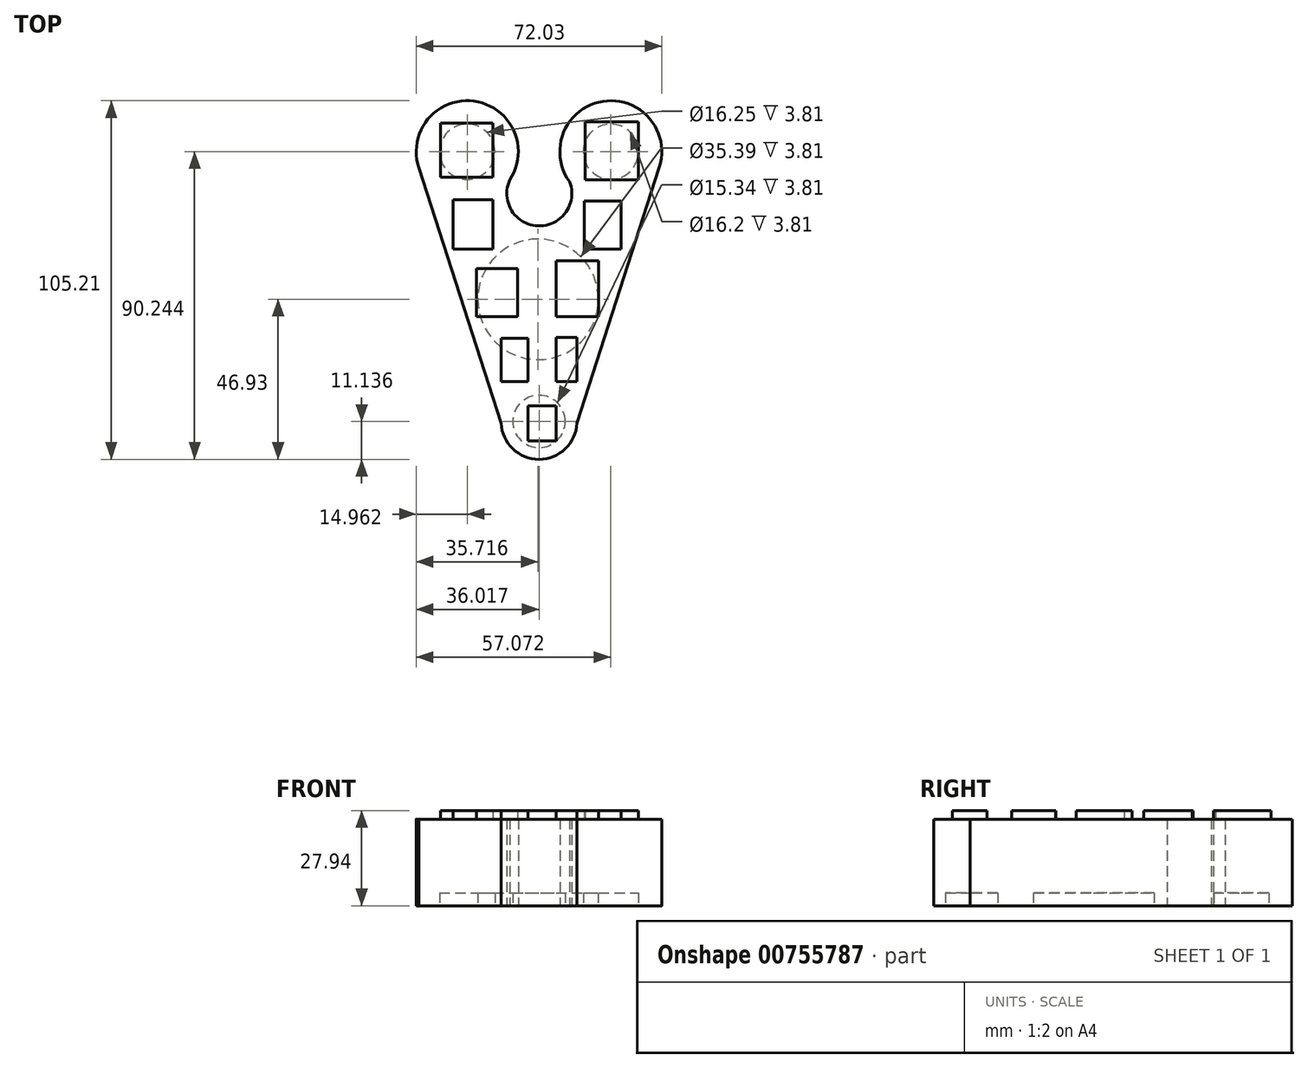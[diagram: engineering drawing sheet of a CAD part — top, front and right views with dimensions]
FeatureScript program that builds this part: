
annotation { "Feature Type Name" : "Feature", "Feature Type Description" : "" }
export const myFeature = defineFeature(function(context is Context, id is Id, definition is map)
    precondition{}
    {
        {
            var Q0;
            Q0=qCreatedBy(makeId("Top.planeOp"),FACE);
            var sketch = newSketch(context, id + "F0", { "sketchPlane" : qUnion([Q0])});
            skCircle(sketch, "E0", {"center": v(-26.02, 32.03) * mm, "radius": 14.96 * mm});
            skLineSegment(sketch, "E1", {"start": v(-4.96, 44.07) * mm, "end": v(-4.96, -47.07) * mm});
            skCircle(sketch, "E2.MirrorC", {"center": v(16.1, 32.03) * mm, "radius": 14.96 * mm});
            skCircle(sketch, "E3", {"center": v(-4.96, -47.07) * mm, "radius": 11.13 * mm});
            skLineSegment(sketch, "E4", {"start": v(-40.21, 27.3) * mm, "end": v(-14.26, -53.2) * mm});
            skLineSegment(sketch, "E5", {"start": v(4.34, -53.2) * mm, "end": v(30.33, 27.44) * mm});
            skArc(sketch, "E6", {"start": v(-13.52, 23.8) * mm, "mid": v(-5.2, 10.26) * mm, "end": v(3.98, 23.25) * mm});
            skSolve(sketch);
        }
        {
            var Q0;
            Q0 = qSketchRegion(id + "F0", true);
            extrude(context, id + "F1", {"entities" : qUnion([Q0]), "depth" : 19.05 * mm, "offsetDistance" : 25.4 * mm});
        }
        {
            var Q0;
            Q0=makeQuery(id+"F1.opExtrude","CAP_FACE",FACE,{"disambiguationData":[OSD([sQuery(id+"F0.wireOp",EDGE,"E0"),sQuery(id+"F0.wireOp",EDGE,"E2.MirrorC"),sQuery(id+"F0.wireOp",EDGE,"E3"),sQuery(id+"F0.wireOp",EDGE,"E4"),sQuery(id+"F0.wireOp",EDGE,"E5"),sQuery(id+"F0.wireOp",EDGE,"E6")])],"isStart":true});
            var sketch = newSketch(context, id + "F2", { "sketchPlane" : qUnion([Q0])});
            skCircle(sketch, "E7", {"center": v(-26.02, -32.03) * mm, "radius": 8.13 * mm});
            skCircle(sketch, "E8", {"center": v(16.1, -32.03) * mm, "radius": 8.1 * mm});
            skCircle(sketch, "E9", {"center": v(-4.96, 47.07) * mm, "radius": 7.67 * mm});
            skCircle(sketch, "E10", {"center": v(-5.26, 11.28) * mm, "radius": 17.7 * mm});
            skSolve(sketch);
        }
        {
            var Q0;
            Q0 = qSketchRegion(id + "F2", true);
            extrude(context, id + "F3", {"entities" : qUnion([Q0]), "operationType" : NewBodyOperationType.REMOVE, "oppositeDirection" : true, "depth" : 3.8 * mm, "offsetDistance" : 25.4 * mm});
        }
        {
            var Q0;
            Q0=makeQuery(id+"F1.opExtrude","CAP_FACE",FACE,{"disambiguationData":[OSD([sQuery(id+"F0.wireOp",EDGE,"E0"),sQuery(id+"F0.wireOp",EDGE,"E2.MirrorC"),sQuery(id+"F0.wireOp",EDGE,"E3"),sQuery(id+"F0.wireOp",EDGE,"E4"),sQuery(id+"F0.wireOp",EDGE,"E5"),sQuery(id+"F0.wireOp",EDGE,"E6")])],"isStart":false});
            extrude(context, id + "F4", {"entities" : qUnion([Q0]), "operationType" : NewBodyOperationType.ADD, "depth" : 6.35 * mm, "offsetDistance" : 25.4 * mm});
        }
        {
            var Q0;
            Q0=makeQuery(id+"F4.opExtrude","CAP_FACE",FACE,{"disambiguationData":[OSD([sQuery(id+"F0.wireOp",EDGE,"E0"),sQuery(id+"F0.wireOp",EDGE,"E2.MirrorC"),sQuery(id+"F0.wireOp",EDGE,"E3"),sQuery(id+"F0.wireOp",EDGE,"E4"),sQuery(id+"F0.wireOp",EDGE,"E5"),sQuery(id+"F0.wireOp",EDGE,"E6")])],"isStart":false});
            var sketch = newSketch(context, id + "F5", { "sketchPlane" : qUnion([Q0])});
            skLineSegment(sketch, "E11.bottom", {"start": v(-33.84, 40.46) * mm, "end": v(-18.5, 40.46) * mm});
            skLineSegment(sketch, "E11.top", {"start": v(-33.84, 24.51) * mm, "end": v(-18.5, 24.51) * mm});
            skLineSegment(sketch, "E11.left", {"start": v(-33.84, 40.46) * mm, "end": v(-33.84, 24.51) * mm});
            skLineSegment(sketch, "E11.right", {"start": v(-18.5, 40.46) * mm, "end": v(-18.5, 24.51) * mm});
            skLineSegment(sketch, "E12.bottom", {"start": v(8.57, 40.76) * mm, "end": v(24.21, 40.76) * mm});
            skLineSegment(sketch, "E12.top", {"start": v(8.57, 23.8) * mm, "end": v(24.21, 23.8) * mm});
            skLineSegment(sketch, "E12.left", {"start": v(8.57, 40.76) * mm, "end": v(8.57, 23.8) * mm});
            skLineSegment(sketch, "E12.right", {"start": v(24.21, 40.76) * mm, "end": v(24.21, 23.8) * mm});
            skLineSegment(sketch, "E13.bottom", {"start": v(-30.23, 17.9) * mm, "end": v(-18.5, 17.9) * mm});
            skLineSegment(sketch, "E13.top", {"start": v(-30.23, 3.46) * mm, "end": v(-18.5, 3.46) * mm});
            skLineSegment(sketch, "E13.left", {"start": v(-30.23, 17.9) * mm, "end": v(-30.23, 3.46) * mm});
            skLineSegment(sketch, "E13.right", {"start": v(-18.5, 17.9) * mm, "end": v(-18.5, 3.46) * mm});
            skLineSegment(sketch, "E14.bottom", {"start": v(8.27, 17.6) * mm, "end": v(19.1, 17.6) * mm});
            skLineSegment(sketch, "E14.top", {"start": v(8.27, 3.46) * mm, "end": v(19.1, 3.46) * mm});
            skLineSegment(sketch, "E14.left", {"start": v(8.27, 17.6) * mm, "end": v(8.27, 3.46) * mm});
            skLineSegment(sketch, "E14.right", {"start": v(19.1, 17.6) * mm, "end": v(19.1, 3.46) * mm});
            skLineSegment(sketch, "E15.bottom", {"start": v(-23.31, -2.26) * mm, "end": v(-11.28, -2.26) * mm});
            skLineSegment(sketch, "E15.top", {"start": v(-23.31, -16.4) * mm, "end": v(-11.28, -16.4) * mm});
            skLineSegment(sketch, "E15.left", {"start": v(-23.31, -2.26) * mm, "end": v(-23.31, -16.4) * mm});
            skLineSegment(sketch, "E15.right", {"start": v(-11.28, -2.26) * mm, "end": v(-11.28, -16.4) * mm});
            skLineSegment(sketch, "E16.bottom", {"start": v(12.48, 0) * mm, "end": v(0, 0) * mm});
            skLineSegment(sketch, "E16.top", {"start": v(12.48, -16.4) * mm, "end": v(0, -16.4) * mm});
            skLineSegment(sketch, "E16.left", {"start": v(12.48, 0) * mm, "end": v(12.48, -16.4) * mm});
            skLineSegment(sketch, "E16.right", {"start": v(0, 0) * mm, "end": v(0, -16.4) * mm});
            skLineSegment(sketch, "E17.bottom", {"start": v(-16.09, -22.7) * mm, "end": v(-8.27, -22.7) * mm});
            skLineSegment(sketch, "E17.top", {"start": v(-16.09, -35.34) * mm, "end": v(-8.27, -35.34) * mm});
            skLineSegment(sketch, "E17.left", {"start": v(-16.09, -22.7) * mm, "end": v(-16.09, -35.34) * mm});
            skLineSegment(sketch, "E17.right", {"start": v(-8.27, -22.7) * mm, "end": v(-8.27, -35.34) * mm});
            skLineSegment(sketch, "E18.bottom", {"start": v(0, -22.4) * mm, "end": v(6.16, -22.4) * mm});
            skLineSegment(sketch, "E18.top", {"start": v(0, -35.34) * mm, "end": v(6.16, -35.34) * mm});
            skLineSegment(sketch, "E18.left", {"start": v(0, -22.4) * mm, "end": v(0, -35.34) * mm});
            skLineSegment(sketch, "E18.right", {"start": v(6.16, -22.4) * mm, "end": v(6.16, -35.34) * mm});
            skLineSegment(sketch, "E19.bottom", {"start": v(-8.27, -42.56) * mm, "end": v(0, -42.56) * mm});
            skLineSegment(sketch, "E19.top", {"start": v(-8.27, -52.79) * mm, "end": v(0, -52.79) * mm});
            skLineSegment(sketch, "E19.left", {"start": v(-8.27, -42.56) * mm, "end": v(-8.27, -52.79) * mm});
            skLineSegment(sketch, "E19.right", {"start": v(0, -42.56) * mm, "end": v(0, -52.79) * mm});
            skSolve(sketch);
        }
        {
            var Q0;
            Q0=makeQuery(id+"F5.imprint","IMPRINT",FACE,{"disambiguationData":[TD([[makeQuery(id+"F5.imprint","IMPRINT",EDGE,{"derivedFrom":sQuery(id+"F5.wireOp",EDGE,"E11.bottom")}),-1.0]])]});
            var Q1;
            Q1=makeQuery(id+"F5.imprint","IMPRINT",FACE,{"disambiguationData":[TD([[makeQuery(id+"F5.imprint","IMPRINT",EDGE,{"derivedFrom":sQuery(id+"F5.wireOp",EDGE,"E13.bottom")}),-1.0]])]});
            var Q2;
            Q2=makeQuery(id+"F5.imprint","IMPRINT",FACE,{"disambiguationData":[TD([[makeQuery(id+"F5.imprint","IMPRINT",EDGE,{"derivedFrom":sQuery(id+"F5.wireOp",EDGE,"E15.bottom")}),-1.0]])]});
            var Q3;
            Q3=makeQuery(id+"F5.imprint","IMPRINT",FACE,{"disambiguationData":[TD([[makeQuery(id+"F5.imprint","IMPRINT",EDGE,{"derivedFrom":sQuery(id+"F5.wireOp",EDGE,"E17.bottom")}),-1.0]])]});
            var Q4;
            Q4=makeQuery(id+"F5.imprint","IMPRINT",FACE,{"disambiguationData":[TD([[makeQuery(id+"F5.imprint","IMPRINT",EDGE,{"derivedFrom":sQuery(id+"F5.wireOp",EDGE,"E19.bottom")}),-1.0]])]});
            var Q5;
            Q5=makeQuery(id+"F5.imprint","IMPRINT",FACE,{"disambiguationData":[TD([[makeQuery(id+"F5.imprint","IMPRINT",EDGE,{"derivedFrom":sQuery(id+"F5.wireOp",EDGE,"E18.bottom")}),-1.0]])]});
            var Q6;
            Q6=makeQuery(id+"F5.imprint","IMPRINT",FACE,{"disambiguationData":[TD([[makeQuery(id+"F5.imprint","IMPRINT",EDGE,{"derivedFrom":sQuery(id+"F5.wireOp",EDGE,"E16.bottom")}),1.0]])]});
            var Q7;
            Q7=makeQuery(id+"F5.imprint","IMPRINT",FACE,{"disambiguationData":[TD([[makeQuery(id+"F5.imprint","IMPRINT",EDGE,{"derivedFrom":sQuery(id+"F5.wireOp",EDGE,"E14.bottom")}),-1.0]])]});
            var Q8;
            Q8=makeQuery(id+"F5.imprint","IMPRINT",FACE,{"disambiguationData":[TD([[makeQuery(id+"F5.imprint","IMPRINT",EDGE,{"derivedFrom":sQuery(id+"F5.wireOp",EDGE,"E12.bottom")}),-1.0]])]});
            extrude(context, id + "F6", {"entities" : qUnion([Q0, Q1, Q2, Q3, Q4, Q5, Q6, Q7, Q8]), "operationType" : NewBodyOperationType.ADD, "depth" : 2.54 * mm, "offsetDistance" : 25.4 * mm});
        }
    });
